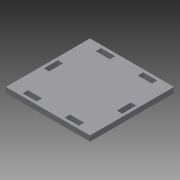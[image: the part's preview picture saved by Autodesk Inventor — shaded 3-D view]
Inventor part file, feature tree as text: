
AUTODESK INVENTOR PART (.ipt)
format: ipt  version: 2015 SP1 (Build 190203100, 203)  size: 152,064 bytes
history: native  units: in
note: dims shown in document units (in); Inventor stores cm internally (conversion verified against a paired STEP export)
features: extrude x2, sketch x2
ambient origin geometry x8: Origin, YZ Plane, XZ Plane, XY Plane, X Axis, Y Axis, Z Axis, Center Point
bodies: Solid1 (feature_tree)
feature tree (4):
  extrude  "Extrusion1"  Depth=3.0in
  extrude  "Extrusion3"  Depth=0.19in
  sketch  "Sketch1"  dims[d0=3.0in d1=3.0in]
  sketch  "Sketch3"  dims[d2=0.5in d3=0.19in d4=0.1in d5=0.5in d6=1.25in d7=0.1in d8=0.19in d9=0.5in d10=0.19in d11=0.0in d12=0.125in d13=0.125in d16=0.1875in d17=0.1875in d18=0.19in d19=0.0in]
